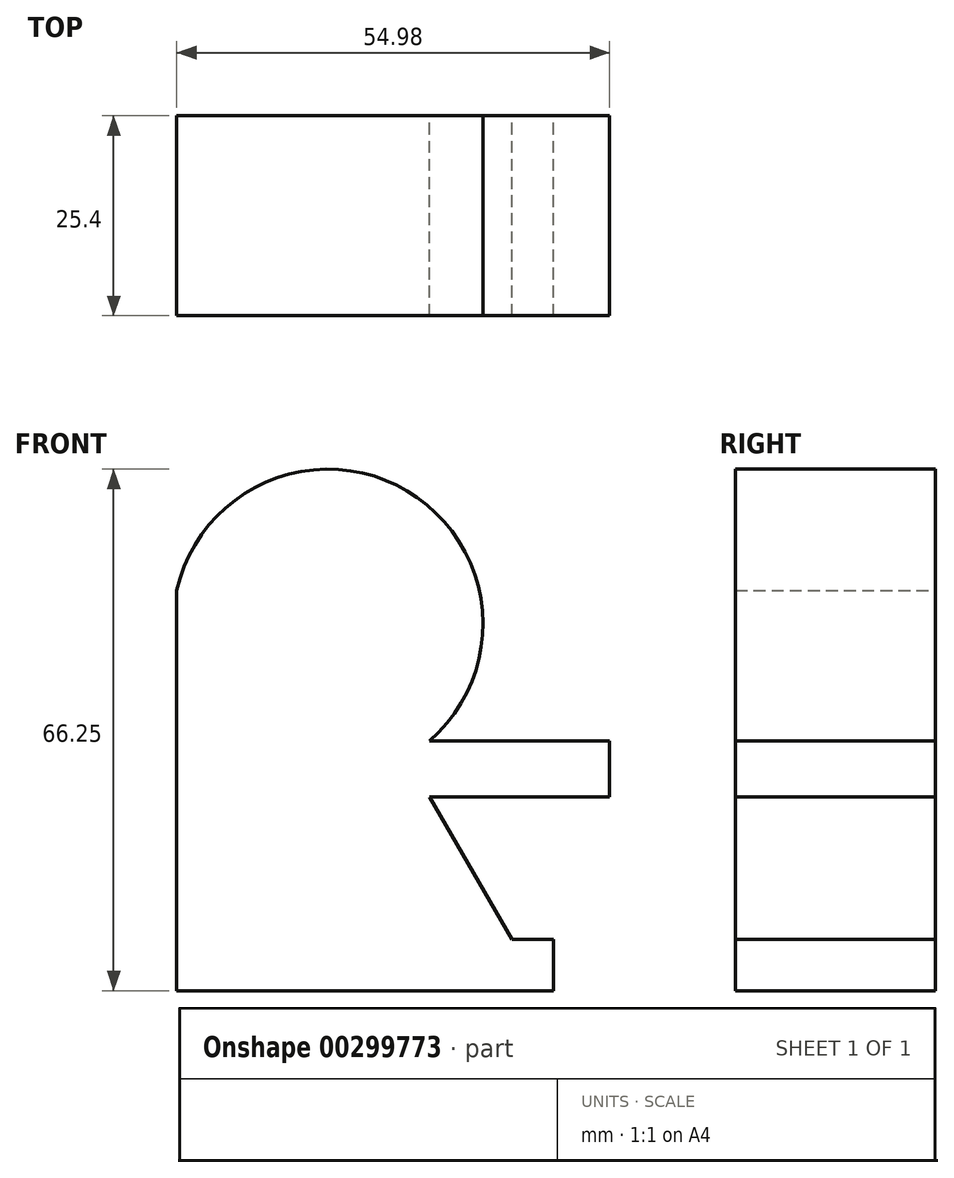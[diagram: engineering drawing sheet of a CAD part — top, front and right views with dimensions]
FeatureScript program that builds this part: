
annotation { "Feature Type Name" : "Feature", "Feature Type Description" : "" }
export const myFeature = defineFeature(function(context is Context, id is Id, definition is map)
    precondition{}
    {
        {
            var Q0;
            Q0=qCreatedBy(makeId("Front.planeOp"),FACE);
            var sketch = newSketch(context, id + "F0", { "sketchPlane" : qUnion([Q0])});
            skLineSegment(sketch, "E0", {"start": v(0, 0) * mm, "end": v(0, 50.84) * mm});
            skArc(sketch, "E1", {"start": v(32.12, 31.73) * mm, "mid": v(29.27, 63.48) * mm, "end": v(0, 50.84) * mm});
            skLineSegment(sketch, "E2", {"start": v(32.12, 31.73) * mm, "end": v(54.98, 31.73) * mm});
            skLineSegment(sketch, "E3", {"start": v(54.98, 31.73) * mm, "end": v(54.98, 24.63) * mm});
            skLineSegment(sketch, "E4", {"start": v(54.98, 24.63) * mm, "end": v(32.12, 24.63) * mm});
            skLineSegment(sketch, "E5", {"start": v(32.12, 24.63) * mm, "end": v(42.57, 6.5) * mm});
            skLineSegment(sketch, "E6", {"start": v(42.57, 6.5) * mm, "end": v(47.89, 6.5) * mm});
            skLineSegment(sketch, "E7", {"start": v(47.89, 6.5) * mm, "end": v(47.89, 0) * mm});
            skLineSegment(sketch, "E8", {"start": v(47.89, 0) * mm, "end": v(0, 0) * mm});
            skSolve(sketch);
        }
        {
            var Q0;
            Q0 = qSketchRegion(id + "F0", true);
            extrude(context, id + "F1", {"entities" : qUnion([Q0]), "depth" : 25.4 * mm});
        }
    });
